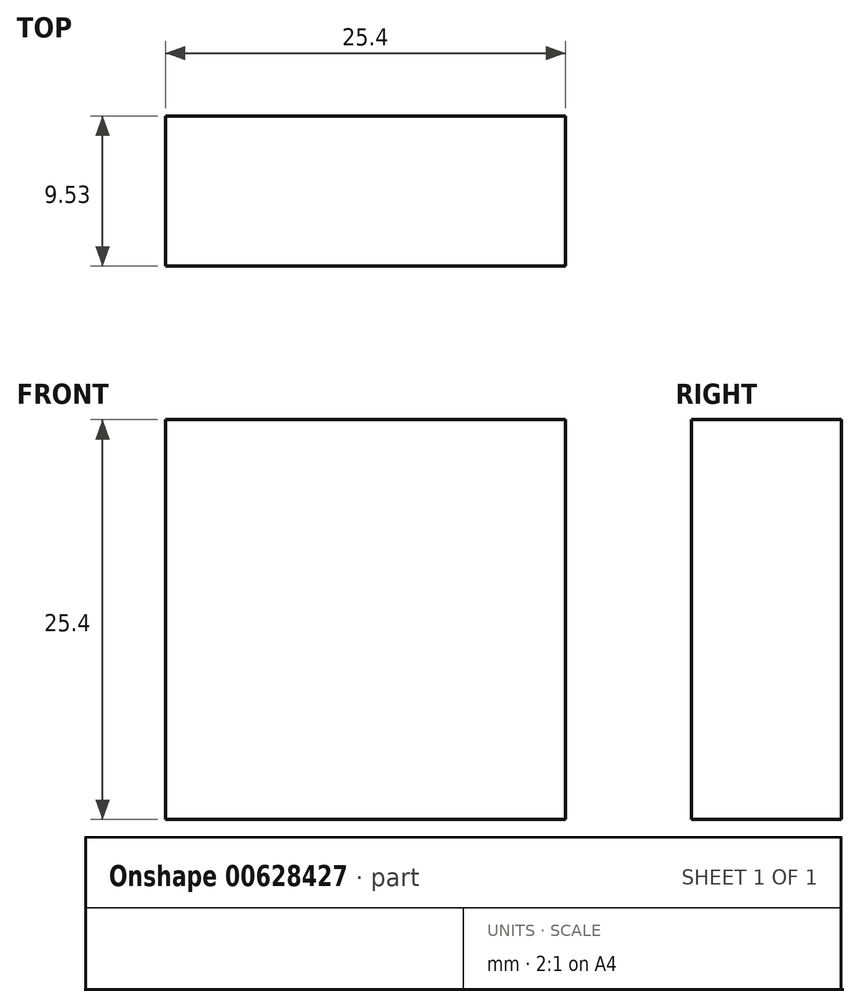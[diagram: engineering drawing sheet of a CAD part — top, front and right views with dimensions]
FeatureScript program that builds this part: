
annotation { "Feature Type Name" : "Feature", "Feature Type Description" : "" }
export const myFeature = defineFeature(function(context is Context, id is Id, definition is map)
    precondition{}
    {
        {
            var Q0;
            Q0=qCreatedBy(makeId("Top.planeOp"),FACE);
            var sketch = newSketch(context, id + "F0", { "sketchPlane" : qUnion([Q0])});
            skLineSegment(sketch, "E0.bottom", {"start": v(0, 0) * mm, "end": v(25.4, 0) * mm});
            skLineSegment(sketch, "E0.top", {"start": v(0, 9.52) * mm, "end": v(25.4, 9.52) * mm});
            skLineSegment(sketch, "E0.left", {"start": v(0, 0) * mm, "end": v(0, 9.52) * mm});
            skLineSegment(sketch, "E0.right", {"start": v(25.4, 0) * mm, "end": v(25.4, 9.52) * mm});
            skSolve(sketch);
        }
        {
            var Q0;
            Q0=makeQuery(id+"F0.imprint","IMPRINT",FACE,{"disambiguationData":[TD([[makeQuery(id+"F0.imprint","IMPRINT",EDGE,{"derivedFrom":sQuery(id+"F0.wireOp",EDGE,"E0.bottom")}),1.0]])]});
            extrude(context, id + "F1", {"entities" : qUnion([Q0]), "depth" : 25.4 * mm, "offsetDistance" : 25.4 * mm});
        }
    });
